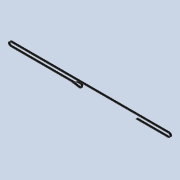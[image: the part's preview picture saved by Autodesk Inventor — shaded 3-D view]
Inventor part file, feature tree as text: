
AUTODESK INVENTOR PART (.ipt)
format: ipt  version: 2020 (Build 240168000, 168)  size: 159,744 bytes
history: native  units: mm
features: sketch x4, reference x4, other x4, extrude x2, sweep x1, projected_geometry x1
ambient origin geometry x8: Origin, YZ Plane, XZ Plane, XY Plane, X Axis, Y Axis, Z Axis, Center Point
bodies: Solid1 (feature_tree), Solid4 (feature_tree)
feature tree (16):
  extrude  "Extrusion1"  Depth=12.0mm
  extrude  "Extrusion3"  Depth=6.0mm TaperAngle=0.0deg
  sweep  "Sweep3"
  sketch  "Sketch1"  dims[d0=526.0mm d1=12.0mm]
  sketch  "Sketch7"  dims[d2=1.0mm d3=6.0mm d4=0.0mm]
  reference  "Reference3"
  reference  "Reference4"
  sketch  "Sketch8"  dims[d11=10.0mm d12=10.0mm]
  reference  "Reference5"
  reference  "Reference6"
  sketch  "Sketch9"  dims[d13=10.0mm d14=0.0mm d15=0.0mm d16=0.0mm]
  projected_geometry  "Projected Loop3"
  parser-record x1  (decoder bookkeeping rows leaked as tree rows — omitted from the tree; the rows remain in map.json)
  other  "0005-10-03 Y axis.iam"
  other  "0005-10-014 Suport Bed.ipt:2"
  other  "0005-10-013 Bed.ipt:7"
note: 1 file-system path scrubbed to <path> (originals preserved in map.json)
